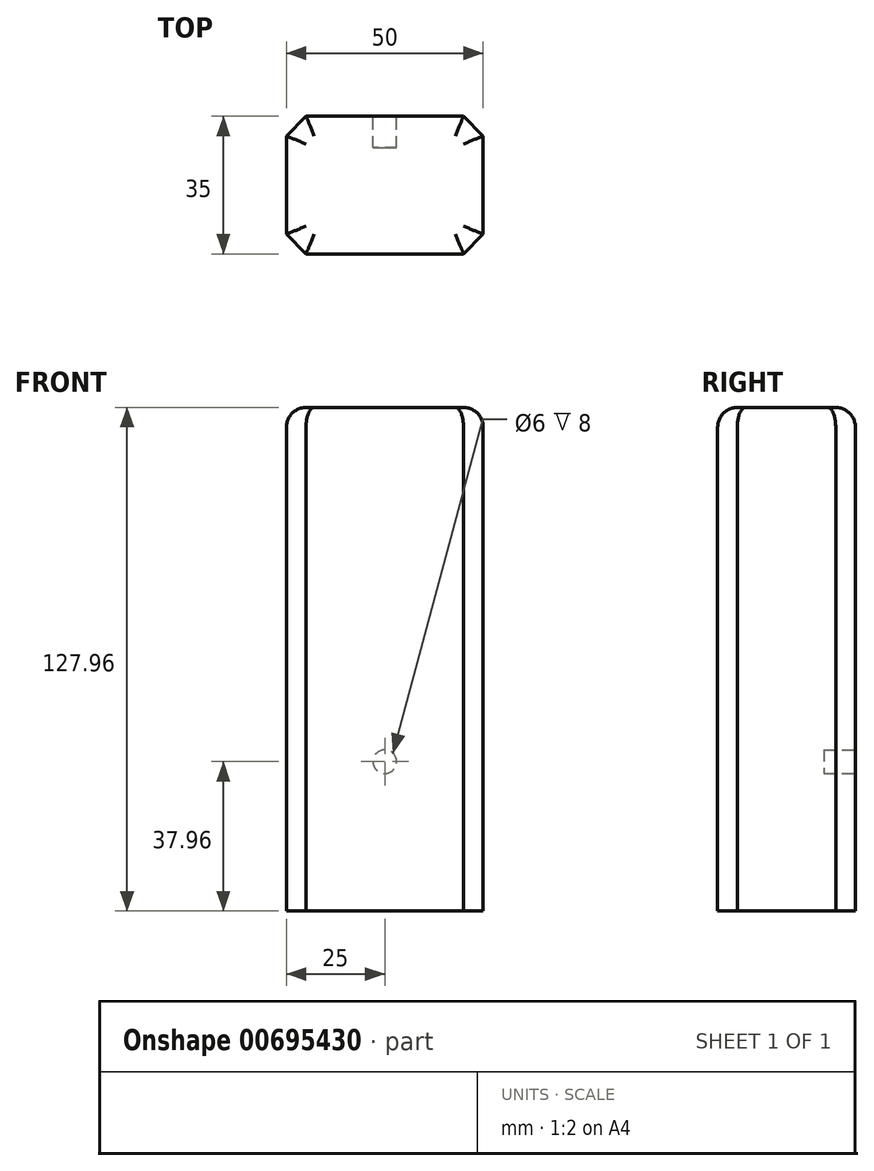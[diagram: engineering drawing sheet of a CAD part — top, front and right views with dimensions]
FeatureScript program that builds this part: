
annotation { "Feature Type Name" : "Feature", "Feature Type Description" : "" }
export const myFeature = defineFeature(function(context is Context, id is Id, definition is map)
    precondition{}
    {
        {
            var Q0;
            Q0=qCreatedBy(makeId("Front.planeOp"),FACE);
            var sketch = newSketch(context, id + "F0", { "sketchPlane" : qUnion([Q0])});
            skLineSegment(sketch, "E0.bottom", {"start": v(-25, 90) * mm, "end": v(25, 90) * mm});
            skLineSegment(sketch, "E0.top", {"start": v(-25, -37.96) * mm, "end": v(25, -37.96) * mm});
            skLineSegment(sketch, "E0.left", {"start": v(-25, 90) * mm, "end": v(-25, -37.96) * mm});
            skLineSegment(sketch, "E0.right", {"start": v(25, 90) * mm, "end": v(25, -37.96) * mm});
            skSolve(sketch);
        }
        {
            var Q0;
            Q0=makeQuery(id+"F0.imprint","IMPRINT",FACE,{"disambiguationData":[TD([[makeQuery(id+"F0.imprint","IMPRINT",EDGE,{"derivedFrom":sQuery(id+"F0.wireOp",EDGE,"E0.bottom")}),-1.0]])]});
            extrude(context, id + "F1", {"entities" : qUnion([Q0]), "depth" : 10 * mm, "offsetDistance" : 25 * mm});
        }
        {
            var Q0;
            Q0=makeQuery(id+"F1.opExtrude","CAP_FACE",FACE,{"disambiguationData":[OSD([sQuery(id+"F0.wireOp",EDGE,"E0.bottom"),sQuery(id+"F0.wireOp",EDGE,"E0.top"),sQuery(id+"F0.wireOp",EDGE,"E0.left"),sQuery(id+"F0.wireOp",EDGE,"E0.right")])],"isStart":true});
            var sketch = newSketch(context, id + "F2", { "sketchPlane" : qUnion([Q0])});
            skCircle(sketch, "E1", {"center": v(0, 0) * mm, "radius": 3 * mm});
            skSolve(sketch);
        }
        {
            var Q0;
            Q0=makeQuery(id+"F2.imprint","IMPRINT",FACE,{"disambiguationData":[TD([[makeQuery(id+"F2.imprint","IMPRINT",EDGE,{"derivedFrom":sQuery(id+"F2.wireOp",EDGE,"E1")}),1.0]])]});
            extrude(context, id + "F3", {"entities" : qUnion([Q0]), "operationType" : NewBodyOperationType.REMOVE, "oppositeDirection" : true, "depth" : 8 * mm, "offsetDistance" : 25 * mm});
        }
        {
            var Q0;
            Q0=makeQuery(id+"F1.opExtrude","CAP_FACE",FACE,{"disambiguationData":[OSD([sQuery(id+"F0.wireOp",EDGE,"E0.bottom"),sQuery(id+"F0.wireOp",EDGE,"E0.top"),sQuery(id+"F0.wireOp",EDGE,"E0.left"),sQuery(id+"F0.wireOp",EDGE,"E0.right")])],"isStart":false});
            extrude(context, id + "F4", {"entities" : qUnion([Q0]), "operationType" : NewBodyOperationType.ADD, "depth" : 25 * mm, "offsetDistance" : 25 * mm});
        }
        {
            var Q0;
            Q0=makeQuery(id+"F1.opExtrude","CAP_EDGE",EDGE,{"disambiguationData":[OSD([sQuery(id+"F0.wireOp",EDGE,"E0.right")])],"isStart":true});
            chamfer(context, id + "F5", {"entities" : qUnion([Q0]), "width" : 5 * mm, "tangentPropagation" : true});
        }
        {
            var Q0;
            Q0=makeQuery(id+"F1.opExtrude","CAP_EDGE",EDGE,{"disambiguationData":[OSD([sQuery(id+"F0.wireOp",EDGE,"E0.left")])],"isStart":true});
            chamfer(context, id + "F6", {"entities" : qUnion([Q0]), "width" : 5 * mm, "tangentPropagation" : true});
        }
        {
            var Q0;
            Q0=makeQuery(id+"F4.opExtrude","CAP_EDGE",EDGE,{"disambiguationData":[OSD([sQuery(id+"F0.wireOp",EDGE,"E0.left")])],"isStart":false});
            chamfer(context, id + "F7", {"entities" : qUnion([Q0]), "width" : 5 * mm, "tangentPropagation" : true});
        }
        {
            var Q0;
            Q0=makeQuery(id+"F4.opExtrude","CAP_EDGE",EDGE,{"disambiguationData":[OSD([sQuery(id+"F0.wireOp",EDGE,"E0.right")])],"isStart":false});
            chamfer(context, id + "F8", {"entities" : qUnion([Q0]), "width" : 5 * mm, "tangentPropagation" : true});
        }
        {
            var Q0;
            {var subQ0=sQuery(id+"F0.wireOp",EDGE,"E0.bottom");Q0=makeQuery(id+"F4.boolean.opBoolean","MERGE",FACE,{"derivedFrom":[makeQuery(id+"F1.opExtrude","SWEPT_FACE",FACE,{"disambiguationData":[OSD([subQ0])]}),makeQuery(id+"F4.opExtrude","SWEPT_FACE",FACE,{"disambiguationData":[OSD([subQ0])]})]});}
            fillet(context, id + "F9", {"entities" : qUnion([Q0]), "radius" : 5 * mm, "tangentPropagation" : true, "allowEdgeOverflow" : false});
        }
    });
